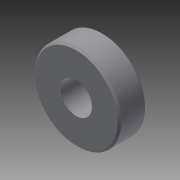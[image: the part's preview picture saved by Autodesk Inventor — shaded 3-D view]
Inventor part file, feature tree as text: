
AUTODESK INVENTOR PART (.ipt)
format: ipt  version: 2013 (Build 170138000, 138)  size: 91,648 bytes
history: native  units: mm
features: revolve x1, sketch x1
ambient origin geometry x8: Origin, YZ Plane, XZ Plane, XY Plane, X Axis, Y Axis, Z Axis, Center Point
bodies: Solid1 (feature_tree)
feature tree (2):
  revolve  "Revolution1"  [1 undecoded]
  sketch  "Sketch1"  dims[d0=0.5mm d1=0.5mm d2=0.5mm d3=0.5mm d4=4.0mm d5=11.0mm d6=7.0mm d7=90.0deg]
note: 1 required parameter value undecoded (feature->parameter linkage not recoverable at this tier; creation-order binding heuristic only, values carry confidence <= 0.55)
